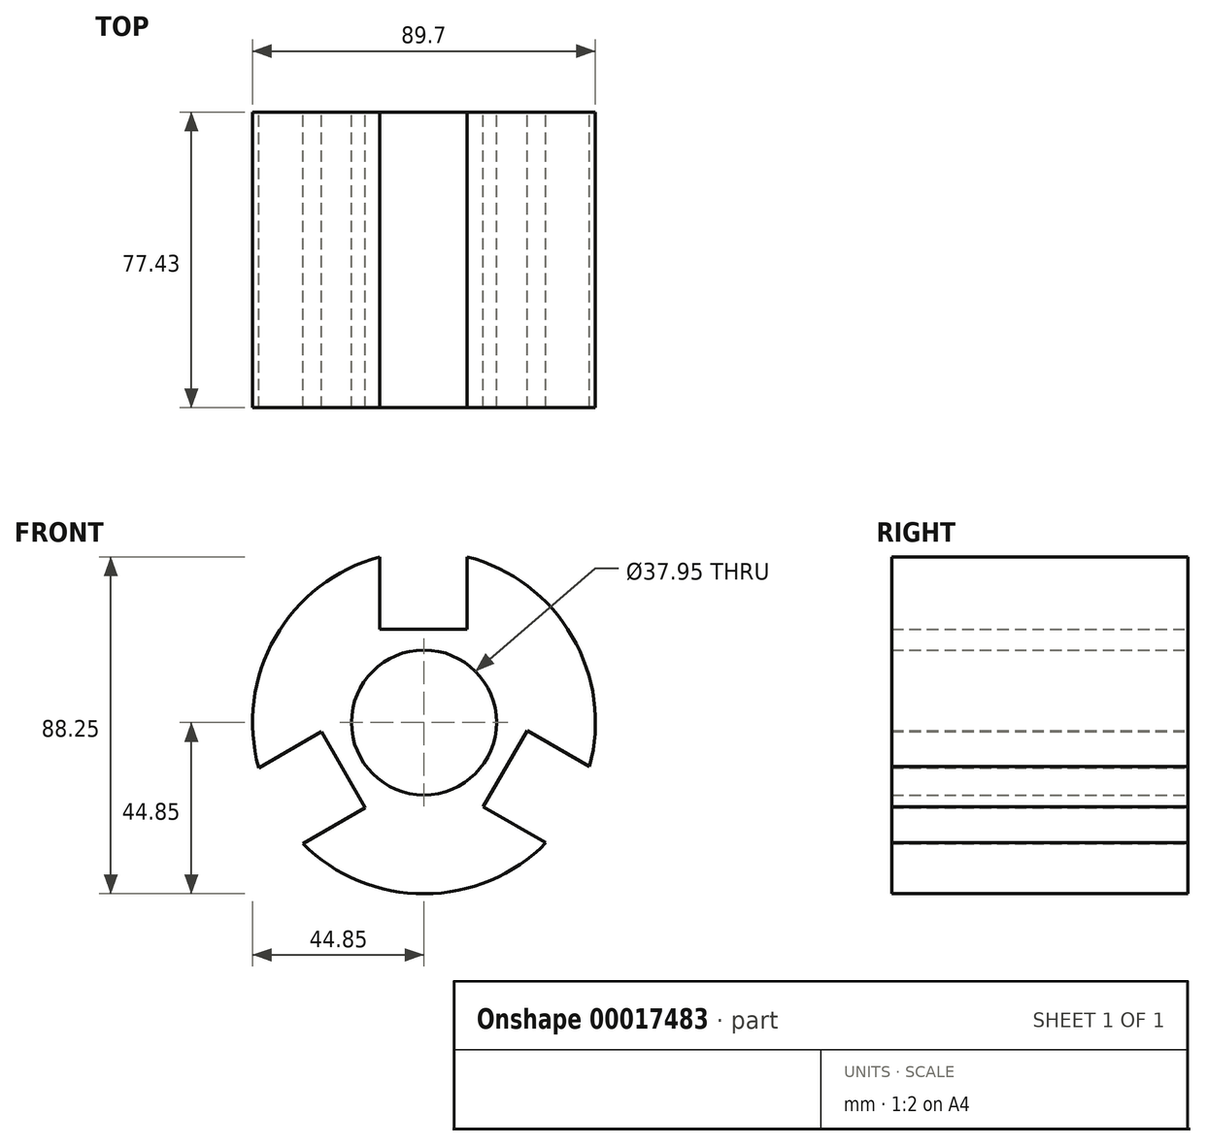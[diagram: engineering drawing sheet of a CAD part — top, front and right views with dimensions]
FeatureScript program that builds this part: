
annotation { "Feature Type Name" : "Feature", "Feature Type Description" : "" }
export const myFeature = defineFeature(function(context is Context, id is Id, definition is map)
    precondition{}
    {
        {
            var Q0;
            Q0=qCreatedBy(makeId("Front.planeOp"),FACE);
            var sketch = newSketch(context, id + "F0", { "sketchPlane" : qUnion([Q0])});
            skCircle(sketch, "E0", {"center": v(0, 0) * mm, "radius": 44.85 * mm});
            skCircle(sketch, "E1", {"center": v(0, 0) * mm, "radius": 18.98 * mm});
            skLineSegment(sketch, "E2", {"start": v(-11.63, 24.44) * mm, "end": v(11.34, 24.44) * mm});
            skLineSegment(sketch, "E3", {"start": v(11.34, 24.44) * mm, "end": v(11.34, 43.4) * mm});
            skLineSegment(sketch, "E4", {"start": v(-11.63, 24.44) * mm, "end": v(-11.63, 43.32) * mm});
            skSolve(sketch);
        }
        {
            var Q0;
            Q0=makeQuery(id+"F0.imprint","IMPRINT",FACE,{"disambiguationData":[TD([[makeQuery(id+"F0.imprint","IMPRINT",EDGE,{"derivedFrom":sQuery(id+"F0.wireOp",EDGE,"E2")}),1.0]])]});
            var Q1;
            Q1=makeQuery(id+"F0.imprint","IMPRINT",FACE,{"disambiguationData":[TD([[makeQuery(id+"F0.imprint","IMPRINT",EDGE,{"derivedFrom":sQuery(id+"F0.wireOp",EDGE,"E1")}),-1.0]])]});
            extrude(context, id + "F1", {"entities" : qUnion([Q0, Q1]), "depth" : 77.43 * mm});
        }
        {
            var Q0;
            Q0=makeQuery(id+"F0.imprint","IMPRINT",FACE,{"disambiguationData":[TD([[makeQuery(id+"F0.imprint","IMPRINT",EDGE,{"derivedFrom":sQuery(id+"F0.wireOp",EDGE,"E2")}),1.0]])]});
            extrude(context, id + "F2", {"entities" : qUnion([Q0]), "operationType" : NewBodyOperationType.REMOVE, "endBound" : BoundingType.THROUGH_ALL, "depth" : 25.4 * mm});
        }
        {
            var Q0;
            Q0=makeQuery(id+"F2.boolean.opBoolean","COPY",FACE,{"derivedFrom":makeQuery(id+"F2.opExtrude","SWEPT_FACE",FACE,{"disambiguationData":[OSD([sQuery(id+"F0.wireOp",EDGE,"E2")])]})});
            var Q1;
            Q1=makeQuery(id+"F2.boolean.opBoolean","COPY",FACE,{"derivedFrom":makeQuery(id+"F2.opExtrude","SWEPT_FACE",FACE,{"disambiguationData":[OSD([sQuery(id+"F0.wireOp",EDGE,"E4")])]})});
            var Q2;
            Q2=makeQuery(id+"F2.boolean.opBoolean","COPY",FACE,{"derivedFrom":makeQuery(id+"F2.opExtrude","SWEPT_FACE",FACE,{"disambiguationData":[OSD([sQuery(id+"F0.wireOp",EDGE,"E3")])]})});
            var Q3;
            Q3=makeQuery(id+"F1.opExtrude","SWEPT_FACE",FACE,{"disambiguationData":[OSD([sQuery(id+"F0.wireOp",EDGE,"E1")])]});
            circularPattern(context, id + "F3", {"faces" : qUnion([Q0, Q1, Q2]), "axis" : qUnion([Q3]), "angle" : 360 * degree, "instanceCount" : 3, "equalSpace" : true, "patternType" : PatternType.FACE});
        }
    });
